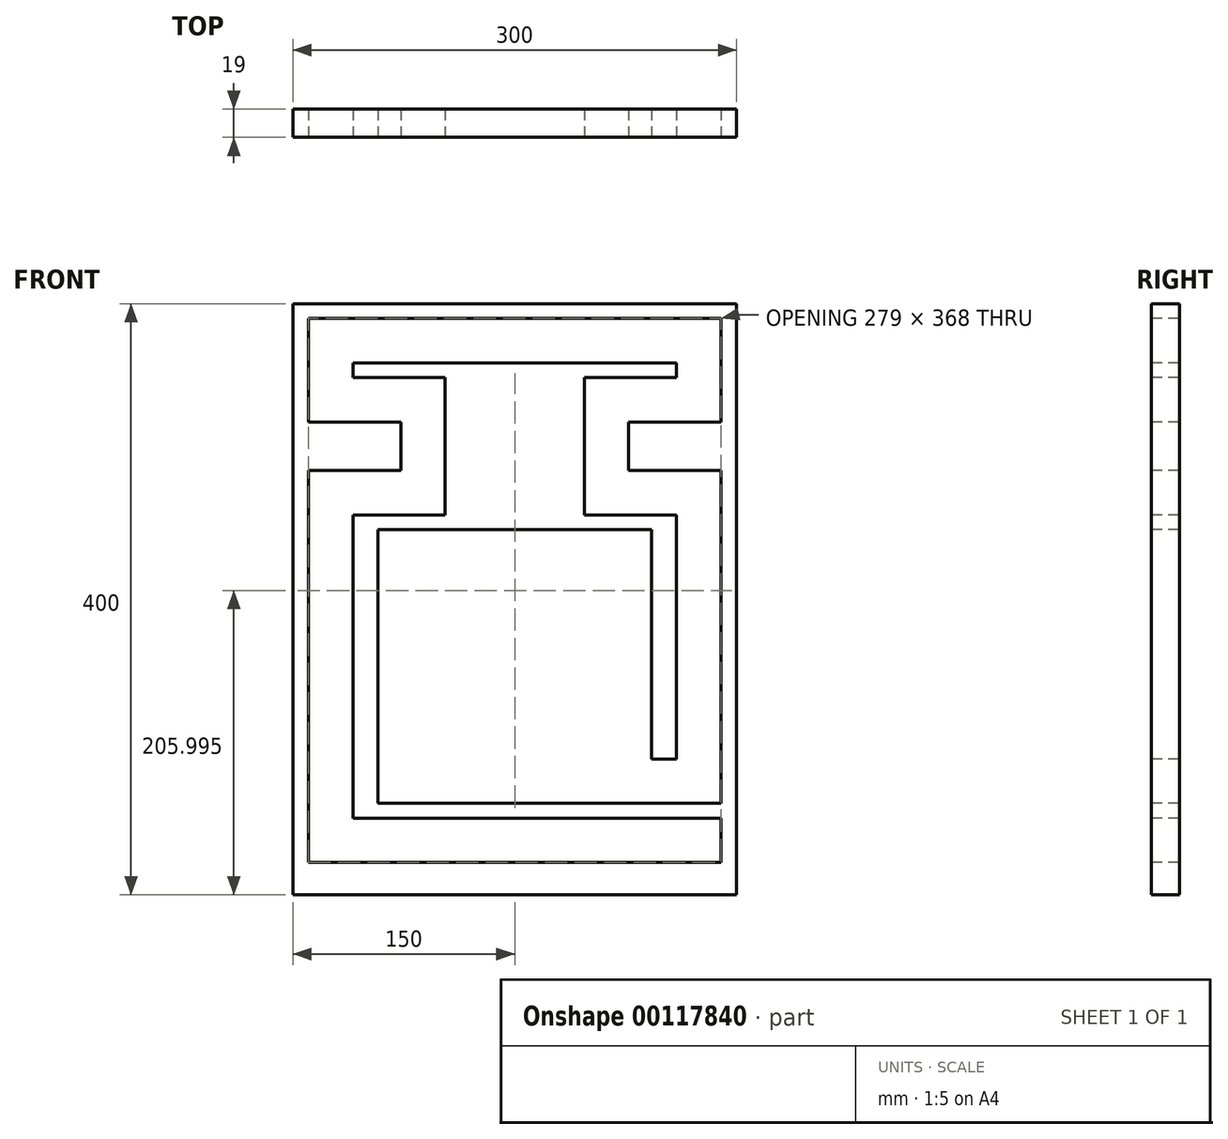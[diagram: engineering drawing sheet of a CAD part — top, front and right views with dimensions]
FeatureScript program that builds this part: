
annotation { "Feature Type Name" : "Feature", "Feature Type Description" : "" }
export const myFeature = defineFeature(function(context is Context, id is Id, definition is map)
    precondition{}
    {
        {
            var Q0;
            Q0=qCreatedBy(makeId("Front.planeOp"),FACE);
            var sketch = newSketch(context, id + "F0", { "sketchPlane" : qUnion([Q0])});
            skLineSegment(sketch, "E0.bottom", {"start": v(-177.42, 198.29) * mm, "end": v(122.58, 198.29) * mm});
            skLineSegment(sketch, "E0.top", {"start": v(-177.42, -201.71) * mm, "end": v(122.58, -201.71) * mm});
            skLineSegment(sketch, "E0.left", {"start": v(-177.42, 198.29) * mm, "end": v(-177.42, -201.71) * mm});
            skLineSegment(sketch, "E0.right", {"start": v(122.58, 198.29) * mm, "end": v(122.58, -201.71) * mm});
            skSolve(sketch);
        }
        {
            var Q0;
            Q0 = qSketchRegion(id + "F0", true);
            extrude(context, id + "F1", {"entities" : qUnion([Q0]), "depth" : 19 * mm});
        }
        {
            var Q0;
            Q0=makeQuery(id+"F1.opExtrude","CAP_FACE",FACE,{"disambiguationData":[OSD([sQuery(id+"F0.wireOp",EDGE,"E0.bottom"),sQuery(id+"F0.wireOp",EDGE,"E0.top"),sQuery(id+"F0.wireOp",EDGE,"E0.left"),sQuery(id+"F0.wireOp",EDGE,"E0.right")])],"isStart":false});
            var sketch = newSketch(context, id + "F2", { "sketchPlane" : qUnion([Q0])});
            skPoint(sketch, "E1.centerSnap0", {"position": v(-27.42, 198.29) * mm});
            skLineSegment(sketch, "E2", {"start": v(112.08, -179.71) * mm, "end": v(112.08, -149.71) * mm});
            skLineSegment(sketch, "E3", {"start": v(112.08, -149.71) * mm, "end": v(-136.92, -149.71) * mm});
            skLineSegment(sketch, "E4", {"start": v(-136.92, -149.71) * mm, "end": v(-136.92, 55.29) * mm});
            skLineSegment(sketch, "E5", {"start": v(-136.92, 55.29) * mm, "end": v(-74.42, 55.29) * mm});
            skLineSegment(sketch, "E6", {"start": v(-74.42, 55.29) * mm, "end": v(-74.42, 148.29) * mm});
            skLineSegment(sketch, "E7", {"start": v(-74.42, 148.29) * mm, "end": v(-136.92, 148.29) * mm});
            skLineSegment(sketch, "E8", {"start": v(-136.92, 148.29) * mm, "end": v(-136.92, 158.29) * mm});
            skLineSegment(sketch, "E9", {"start": v(-136.92, 158.29) * mm, "end": v(82.08, 158.29) * mm});
            skLineSegment(sketch, "E10", {"start": v(82.08, 158.29) * mm, "end": v(82.08, 148.29) * mm});
            skLineSegment(sketch, "E11", {"start": v(82.08, 148.29) * mm, "end": v(19.58, 148.29) * mm});
            skLineSegment(sketch, "E12", {"start": v(19.58, 148.29) * mm, "end": v(19.58, 55.29) * mm});
            skLineSegment(sketch, "E13", {"start": v(19.58, 55.29) * mm, "end": v(82.08, 55.29) * mm});
            skLineSegment(sketch, "E14", {"start": v(82.08, 55.29) * mm, "end": v(82.08, -109.71) * mm});
            skLineSegment(sketch, "E15", {"start": v(82.08, -109.71) * mm, "end": v(65.08, -109.71) * mm});
            skLineSegment(sketch, "E16", {"start": v(65.08, -109.71) * mm, "end": v(65.08, 45.29) * mm});
            skLineSegment(sketch, "E17", {"start": v(65.08, 45.29) * mm, "end": v(-119.92, 45.29) * mm});
            skLineSegment(sketch, "E18", {"start": v(-119.92, 45.29) * mm, "end": v(-119.92, -139.71) * mm});
            skLineSegment(sketch, "E19", {"start": v(-119.92, -139.71) * mm, "end": v(112.08, -139.71) * mm});
            skLineSegment(sketch, "E20", {"start": v(112.08, -139.71) * mm, "end": v(112.08, 85.29) * mm});
            skLineSegment(sketch, "E21", {"start": v(112.08, 85.29) * mm, "end": v(49.58, 85.29) * mm});
            skLineSegment(sketch, "E22", {"start": v(49.58, 85.29) * mm, "end": v(49.58, 118.29) * mm});
            skLineSegment(sketch, "E23", {"start": v(49.58, 118.29) * mm, "end": v(112.08, 118.29) * mm});
            skLineSegment(sketch, "E24", {"start": v(112.08, 118.29) * mm, "end": v(112.08, 188.29) * mm});
            skLineSegment(sketch, "E25", {"start": v(112.08, 188.29) * mm, "end": v(-166.92, 188.29) * mm});
            skLineSegment(sketch, "E26", {"start": v(-166.92, 188.29) * mm, "end": v(-166.92, 118.29) * mm});
            skLineSegment(sketch, "E27", {"start": v(-166.92, 118.29) * mm, "end": v(-104.42, 118.29) * mm});
            skLineSegment(sketch, "E28", {"start": v(-104.42, 118.29) * mm, "end": v(-104.42, 85.29) * mm});
            skLineSegment(sketch, "E29", {"start": v(-104.42, 85.29) * mm, "end": v(-166.92, 85.29) * mm});
            skLineSegment(sketch, "E30", {"start": v(-166.92, 85.29) * mm, "end": v(-166.92, -179.71) * mm});
            skLineSegment(sketch, "E31", {"start": v(-166.92, -179.71) * mm, "end": v(112.08, -179.71) * mm});
            skSolve(sketch);
        }
        {
            var Q0;
            Q0 = qSketchRegion(id + "F2", true);
            extrude(context, id + "F3", {"entities" : qUnion([Q0]), "operationType" : NewBodyOperationType.REMOVE, "oppositeDirection" : true, "depth" : 19 * mm});
        }
    });
